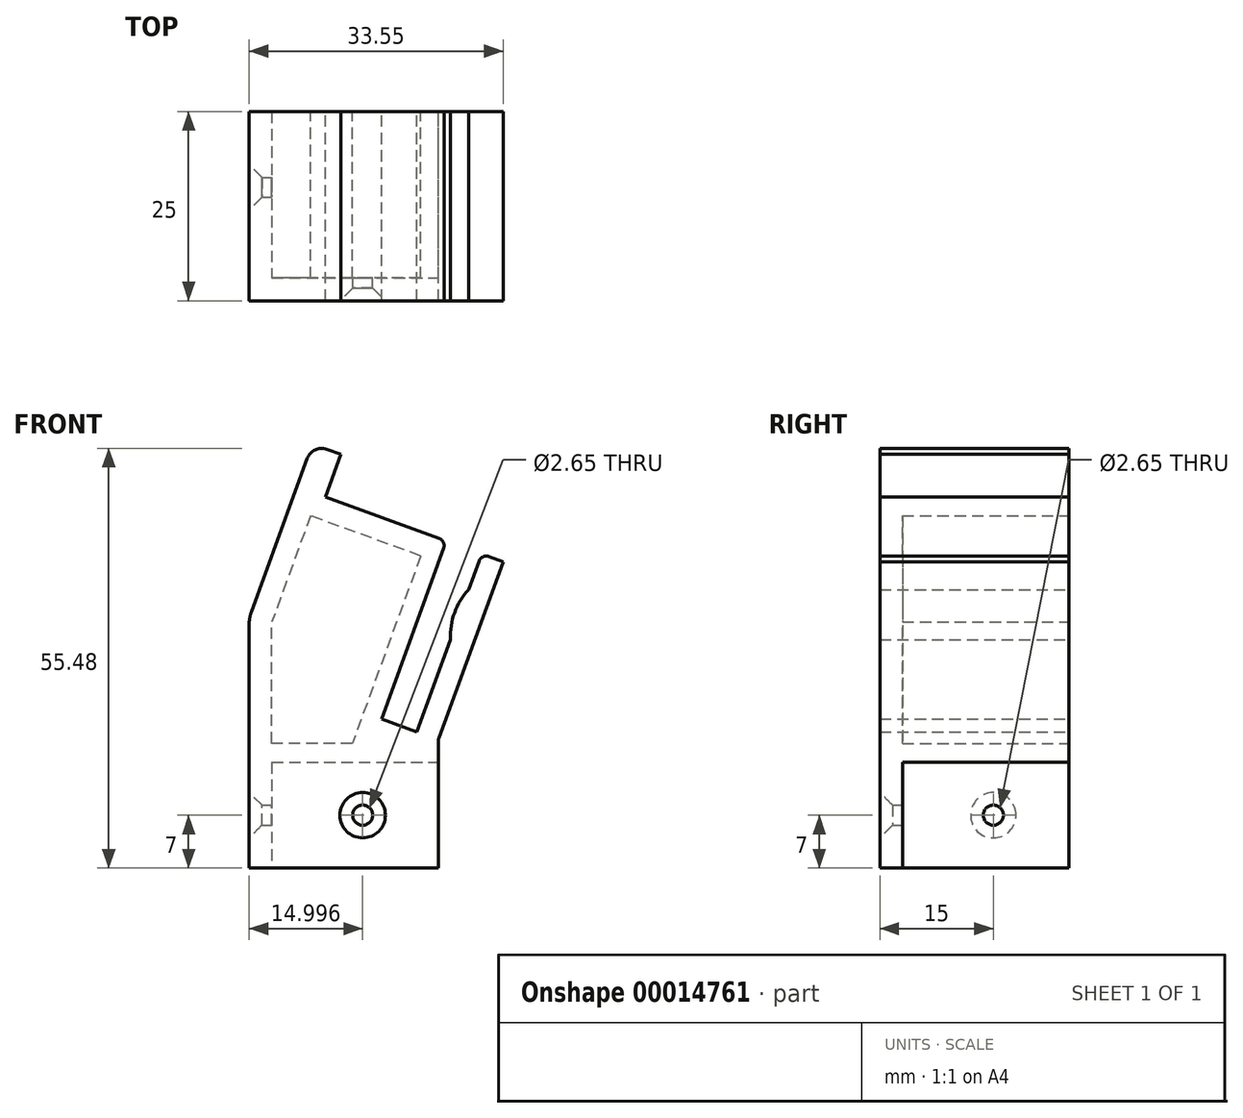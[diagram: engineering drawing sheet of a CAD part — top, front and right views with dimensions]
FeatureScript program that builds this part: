
annotation { "Feature Type Name" : "Feature", "Feature Type Description" : "" }
export const myFeature = defineFeature(function(context is Context, id is Id, definition is map)
    precondition{}
    {
        {
            var Q0;
            Q0=qCreatedBy(makeId("Front.planeOp"),FACE);
            var sketch = newSketch(context, id + "F0", { "sketchPlane" : qUnion([Q0])});
            skLineSegment(sketch, "E0", {"start": v(-18.57, 0) * mm, "end": v(-18.57, 18.15) * mm});
            skLineSegment(sketch, "E1", {"start": v(-8.32, 41.36) * mm, "end": v(-6.46, 40.68) * mm});
            skLineSegment(sketch, "E2", {"start": v(-6.46, 40.68) * mm, "end": v(-8.52, 35.04) * mm});
            skLineSegment(sketch, "E3", {"start": v(-8.52, 35.04) * mm, "end": v(6.52, 29.57) * mm});
            skLineSegment(sketch, "E4", {"start": v(7.12, 28.29) * mm, "end": v(-1.1, 5.74) * mm});
            skLineSegment(sketch, "E5", {"start": v(-1.1, 5.74) * mm, "end": v(3.6, 4.03) * mm});
            skLineSegment(sketch, "E6", {"start": v(3.6, 4.03) * mm, "end": v(8.04, 16.2) * mm});
            skArc(sketch, "E7", {"start": v(10.45, 22.82) * mm, "mid": v(8.56, 19.76) * mm, "end": v(8.04, 16.2) * mm});
            skLineSegment(sketch, "E8", {"start": v(10.45, 22.82) * mm, "end": v(11.82, 26.58) * mm});
            skLineSegment(sketch, "E9", {"start": v(13.1, 27.18) * mm, "end": v(14.98, 26.5) * mm});
            skLineSegment(sketch, "E10", {"start": v(14.98, 26.5) * mm, "end": v(6.49, 3.17) * mm});
            skLineSegment(sketch, "E11", {"start": v(6.43, 2.82) * mm, "end": v(6.43, 0) * mm});
            skLineSegment(sketch, "E12", {"start": v(6.43, 0) * mm, "end": v(-18.57, 0) * mm});
            skLineSegment(sketch, "E13", {"start": v(7.46, 29.23) * mm, "end": v(11.02, 27.93) * mm, "construction": true});
            skLineSegment(sketch, "E14", {"start": v(3.6, 4.03) * mm, "end": v(9.61, 1.84) * mm, "construction": true});
            skLineSegment(sketch, "E15", {"start": v(-10.88, 40.16) * mm, "end": v(-18.27, 19.86) * mm});
            skPoint(sketch, "E15.endSnap0", {"position": v(-18.57, 19.9) * mm});
            skPoint(sketch, "E16.orphan", {"position": v(-18.57, 39.81) * mm});
            skLineSegment(sketch, "E17", {"start": v(-18.57, 0) * mm, "end": v(-18.57, -14) * mm});
            skLineSegment(sketch, "E18", {"start": v(-18.57, -14) * mm, "end": v(6.43, -14) * mm});
            skLineSegment(sketch, "E19", {"start": v(6.43, -14) * mm, "end": v(6.43, 0) * mm});
            skPoint(sketch, "E20.visualSharp", {"position": v(-18.57, 19.04) * mm});
            skArc(sketch, "E20.filletArc", {"start": v(-18.27, 19.86) * mm, "mid": v(-18.5, 19.02) * mm, "end": v(-18.57, 18.15) * mm});
            skPoint(sketch, "E21.visualSharp", {"position": v(-10.2, 42.04) * mm});
            skArc(sketch, "E21.filletArc", {"start": v(-8.32, 41.36) * mm, "mid": v(-9.85, 41.3) * mm, "end": v(-10.88, 40.16) * mm});
            skPoint(sketch, "E22.visualSharp", {"position": v(12.16, 27.52) * mm});
            skArc(sketch, "E22.filletArc", {"start": v(13.1, 27.18) * mm, "mid": v(12.33, 27.14) * mm, "end": v(11.82, 26.58) * mm});
            skPoint(sketch, "E23.visualSharp", {"position": v(7.46, 29.23) * mm});
            skArc(sketch, "E23.filletArc", {"start": v(7.12, 28.29) * mm, "mid": v(7.08, 29.05) * mm, "end": v(6.52, 29.57) * mm});
            skPoint(sketch, "E24.visualSharp", {"position": v(6.43, 3) * mm});
            skArc(sketch, "E24.filletArc", {"start": v(6.49, 3.17) * mm, "mid": v(6.44, 3) * mm, "end": v(6.43, 2.82) * mm});
            skSolve(sketch);
        }
        {
            var Q0;
            Q0=makeQuery(id+"F0.imprint","IMPRINT",FACE,{"disambiguationData":[TD([[makeQuery(id+"F0.imprint","IMPRINT",EDGE,{"derivedFrom":sQuery(id+"F0.wireOp",EDGE,"E0")}),-1.0]])]});
            var Q1;
            Q1=makeQuery(id+"F0.imprint","IMPRINT",FACE,{"disambiguationData":[TD([[makeQuery(id+"F0.imprint","IMPRINT",EDGE,{"derivedFrom":sQuery(id+"F0.wireOp",EDGE,"E12")}),1.0]])]});
            extrude(context, id + "F1", {"entities" : qUnion([Q0, Q1]), "depth" : 25 * mm});
        }
        {
            var Q0;
            Q0=makeQuery(id+"F1.opExtrude","SWEPT_FACE",FACE,{"disambiguationData":[OSD([sQuery(id+"F0.wireOp",EDGE,"E18")])]});
            var sketch = newSketch(context, id + "F2", { "sketchPlane" : qUnion([Q0])});
            skLineSegment(sketch, "E25.bottom", {"start": v(-15.57, 0) * mm, "end": v(6.43, 0) * mm});
            skLineSegment(sketch, "E25.top", {"start": v(-15.57, 22) * mm, "end": v(6.43, 22) * mm});
            skLineSegment(sketch, "E25.left", {"start": v(-15.57, 0) * mm, "end": v(-15.57, 22) * mm});
            skLineSegment(sketch, "E25.right", {"start": v(6.43, 0) * mm, "end": v(6.43, 22) * mm});
            skSolve(sketch);
        }
        {
            var Q0;
            Q0=makeQuery(id+"F2.imprint","IMPRINT",FACE,{"disambiguationData":[TD([[makeQuery(id+"F2.imprint","IMPRINT",EDGE,{"derivedFrom":sQuery(id+"F2.wireOp",EDGE,"E25.bottom")}),1.0]])]});
            extrude(context, id + "F3", {"entities" : qUnion([Q0]), "operationType" : NewBodyOperationType.REMOVE, "oppositeDirection" : true, "depth" : 14 * mm});
        }
        {
            var Q0;
            Q0=makeQuery(id+"F1.opExtrude","CAP_FACE",FACE,{"disambiguationData":[OSD([sQuery(id+"F0.wireOp",EDGE,"E0"),sQuery(id+"F0.wireOp",EDGE,"E1"),sQuery(id+"F0.wireOp",EDGE,"E2"),sQuery(id+"F0.wireOp",EDGE,"E3"),sQuery(id+"F0.wireOp",EDGE,"E4"),sQuery(id+"F0.wireOp",EDGE,"E5"),sQuery(id+"F0.wireOp",EDGE,"E6"),sQuery(id+"F0.wireOp",EDGE,"E7"),sQuery(id+"F0.wireOp",EDGE,"E8"),sQuery(id+"F0.wireOp",EDGE,"E9"),sQuery(id+"F0.wireOp",EDGE,"E10"),sQuery(id+"F0.wireOp",EDGE,"E11"),sQuery(id+"F0.wireOp",EDGE,"E15"),sQuery(id+"F0.wireOp",EDGE,"E17"),sQuery(id+"F0.wireOp",EDGE,"E18"),sQuery(id+"F0.wireOp",EDGE,"E19"),sQuery(id+"F0.wireOp",EDGE,"E20.filletArc"),sQuery(id+"F0.wireOp",EDGE,"E21.filletArc"),sQuery(id+"F0.wireOp",EDGE,"E22.filletArc"),sQuery(id+"F0.wireOp",EDGE,"E23.filletArc"),sQuery(id+"F0.wireOp",EDGE,"E24.filletArc")])],"isStart":false});
            var sketch = newSketch(context, id + "F4", { "sketchPlane" : qUnion([Q0])});
            skPoint(sketch, "E26", {"position": v(-3.57, -7) * mm});
            skSolve(sketch);
        }
        {
            var Q0;
            Q0=makeQuery(id+"F1.opExtrude","SWEPT_FACE",FACE,{"disambiguationData":[OSD([sQuery(id+"F0.wireOp",EDGE,"E0"),sQuery(id+"F0.wireOp",EDGE,"E17")])]});
            var sketch = newSketch(context, id + "F5", { "sketchPlane" : qUnion([Q0])});
            skPoint(sketch, "E27", {"position": v(10, -7) * mm});
            skSolve(sketch);
        }
        {
            var Q0;
            Q0=sQuery(id+"F5.wireOp",VERTEX,"E27");
            var Q1;
            Q1=makeQuery(id+"F1.opExtrude","SWEPT_BODY",BODY,{"disambiguationData":[OSD([sQuery(id+"F0.wireOp",EDGE,"E0"),sQuery(id+"F0.wireOp",EDGE,"E1"),sQuery(id+"F0.wireOp",EDGE,"E2"),sQuery(id+"F0.wireOp",EDGE,"E3"),sQuery(id+"F0.wireOp",EDGE,"E4"),sQuery(id+"F0.wireOp",EDGE,"E5"),sQuery(id+"F0.wireOp",EDGE,"E6"),sQuery(id+"F0.wireOp",EDGE,"E7"),sQuery(id+"F0.wireOp",EDGE,"E8"),sQuery(id+"F0.wireOp",EDGE,"E9"),sQuery(id+"F0.wireOp",EDGE,"E10"),sQuery(id+"F0.wireOp",EDGE,"E11"),sQuery(id+"F0.wireOp",EDGE,"E15"),sQuery(id+"F0.wireOp",EDGE,"E17"),sQuery(id+"F0.wireOp",EDGE,"E18"),sQuery(id+"F0.wireOp",EDGE,"E19"),sQuery(id+"F0.wireOp",EDGE,"E20.filletArc"),sQuery(id+"F0.wireOp",EDGE,"E21.filletArc"),sQuery(id+"F0.wireOp",EDGE,"E22.filletArc"),sQuery(id+"F0.wireOp",EDGE,"E23.filletArc"),sQuery(id+"F0.wireOp",EDGE,"E24.filletArc")])]});
            hole(context, id + "F6", {"style" : HoleStyle.C_SINK, "endStyle" : HoleEndStyle.BLIND, "holeDiameter" : 2.65 * mm, "cSinkDiameter" : 6 * mm, "cSinkAngle" : 90 * degree, "holeDepth" : 6 * mm, "locations" : qUnion([Q0]), "scope" : qUnion([Q1]), "startStyle" : HoleStartStyle.SKETCH});
        }
        {
            var Q0;
            Q0=sQuery(id+"F4.wireOp",VERTEX,"E26");
            var Q1;
            Q1=makeQuery(id+"F1.opExtrude","SWEPT_BODY",BODY,{"disambiguationData":[OSD([sQuery(id+"F0.wireOp",EDGE,"E0"),sQuery(id+"F0.wireOp",EDGE,"E1"),sQuery(id+"F0.wireOp",EDGE,"E2"),sQuery(id+"F0.wireOp",EDGE,"E3"),sQuery(id+"F0.wireOp",EDGE,"E4"),sQuery(id+"F0.wireOp",EDGE,"E5"),sQuery(id+"F0.wireOp",EDGE,"E6"),sQuery(id+"F0.wireOp",EDGE,"E7"),sQuery(id+"F0.wireOp",EDGE,"E8"),sQuery(id+"F0.wireOp",EDGE,"E9"),sQuery(id+"F0.wireOp",EDGE,"E10"),sQuery(id+"F0.wireOp",EDGE,"E11"),sQuery(id+"F0.wireOp",EDGE,"E15"),sQuery(id+"F0.wireOp",EDGE,"E17"),sQuery(id+"F0.wireOp",EDGE,"E18"),sQuery(id+"F0.wireOp",EDGE,"E19"),sQuery(id+"F0.wireOp",EDGE,"E20.filletArc"),sQuery(id+"F0.wireOp",EDGE,"E21.filletArc"),sQuery(id+"F0.wireOp",EDGE,"E22.filletArc"),sQuery(id+"F0.wireOp",EDGE,"E23.filletArc"),sQuery(id+"F0.wireOp",EDGE,"E24.filletArc")])]});
            hole(context, id + "F7", {"style" : HoleStyle.C_SINK, "endStyle" : HoleEndStyle.BLIND, "holeDiameter" : 2.65 * mm, "cSinkDiameter" : 6 * mm, "cSinkAngle" : 90 * degree, "holeDepth" : 6 * mm, "locations" : qUnion([Q0]), "scope" : qUnion([Q1]), "startStyle" : HoleStartStyle.SKETCH});
        }
        {
            var Q0;
            Q0=makeQuery(id+"F1.opExtrude","CAP_FACE",FACE,{"disambiguationData":[OSD([sQuery(id+"F0.wireOp",EDGE,"E0"),sQuery(id+"F0.wireOp",EDGE,"E1"),sQuery(id+"F0.wireOp",EDGE,"E2"),sQuery(id+"F0.wireOp",EDGE,"E3"),sQuery(id+"F0.wireOp",EDGE,"E4"),sQuery(id+"F0.wireOp",EDGE,"E5"),sQuery(id+"F0.wireOp",EDGE,"E6"),sQuery(id+"F0.wireOp",EDGE,"E7"),sQuery(id+"F0.wireOp",EDGE,"E8"),sQuery(id+"F0.wireOp",EDGE,"E9"),sQuery(id+"F0.wireOp",EDGE,"E10"),sQuery(id+"F0.wireOp",EDGE,"E11"),sQuery(id+"F0.wireOp",EDGE,"E15"),sQuery(id+"F0.wireOp",EDGE,"E17"),sQuery(id+"F0.wireOp",EDGE,"E18"),sQuery(id+"F0.wireOp",EDGE,"E19"),sQuery(id+"F0.wireOp",EDGE,"E20.filletArc"),sQuery(id+"F0.wireOp",EDGE,"E21.filletArc"),sQuery(id+"F0.wireOp",EDGE,"E22.filletArc"),sQuery(id+"F0.wireOp",EDGE,"E23.filletArc"),sQuery(id+"F0.wireOp",EDGE,"E24.filletArc")])],"isStart":true});
            var sketch = newSketch(context, id + "F8", { "sketchPlane" : qUnion([Q0])});
            skLineSegment(sketch, "E28", {"start": v(-4.08, 27.26) * mm, "end": v(4.93, 2.5) * mm});
            skLineSegment(sketch, "E29", {"start": v(4.93, 2.5) * mm, "end": v(15.57, 2.5) * mm});
            skLineSegment(sketch, "E30", {"start": v(15.57, 2.5) * mm, "end": v(15.57, 18.5) * mm});
            skLineSegment(sketch, "E31", {"start": v(-4.08, 27.26) * mm, "end": v(10.46, 32.56) * mm});
            skLineSegment(sketch, "E32", {"start": v(10.46, 32.56) * mm, "end": v(15.57, 18.5) * mm});
            skSolve(sketch);
        }
        {
            var Q0;
            Q0=makeQuery(id+"F8.imprint","IMPRINT",FACE,{"disambiguationData":[TD([[makeQuery(id+"F8.imprint","IMPRINT",EDGE,{"derivedFrom":sQuery(id+"F8.wireOp",EDGE,"E28")}),1.0]])]});
            extrude(context, id + "F9", {"entities" : qUnion([Q0]), "operationType" : NewBodyOperationType.REMOVE, "oppositeDirection" : true, "depth" : 22 * mm});
        }
    });
